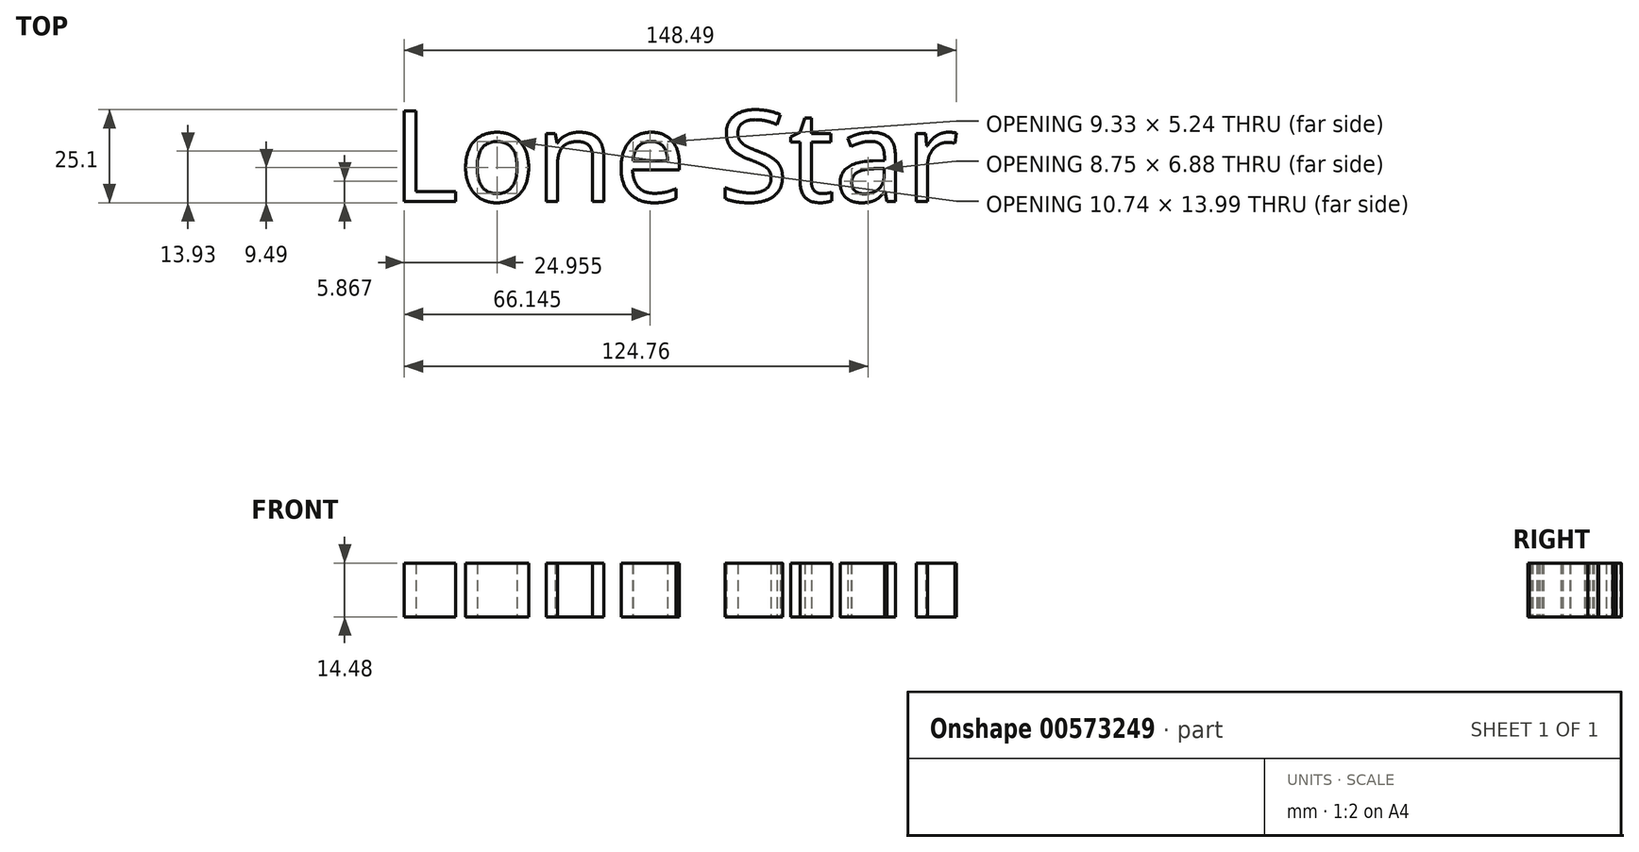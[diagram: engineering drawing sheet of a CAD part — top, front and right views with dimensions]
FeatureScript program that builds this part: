
annotation { "Feature Type Name" : "Feature", "Feature Type Description" : "" }
export const myFeature = defineFeature(function(context is Context, id is Id, definition is map)
    precondition{}
    {
        {
            var Q0;
            Q0=qCreatedBy(makeId("Top.planeOp"),FACE);
            var sketch = newSketch(context, id + "F0", { "sketchPlane" : qUnion([Q0])});
            skText(sketch, "E0", { "text": "Lone Star", "fontName": "NotoSans-Regular.ttf"});
            const initialGuessF0  = {"E0": [-0.0773, 0, 1, 0, 0.02462]};
            skSetInitialGuess(sketch, initialGuessF0);
            skSolve(sketch);
        }
        {
            var Q0;
            Q0 = qSketchRegion(id + "F0", true);
            extrude(context, id + "F1", {"entities" : qUnion([Q0]), "depth" : 14.48 * mm, "offsetDistance" : 25.4 * mm});
        }
    });
